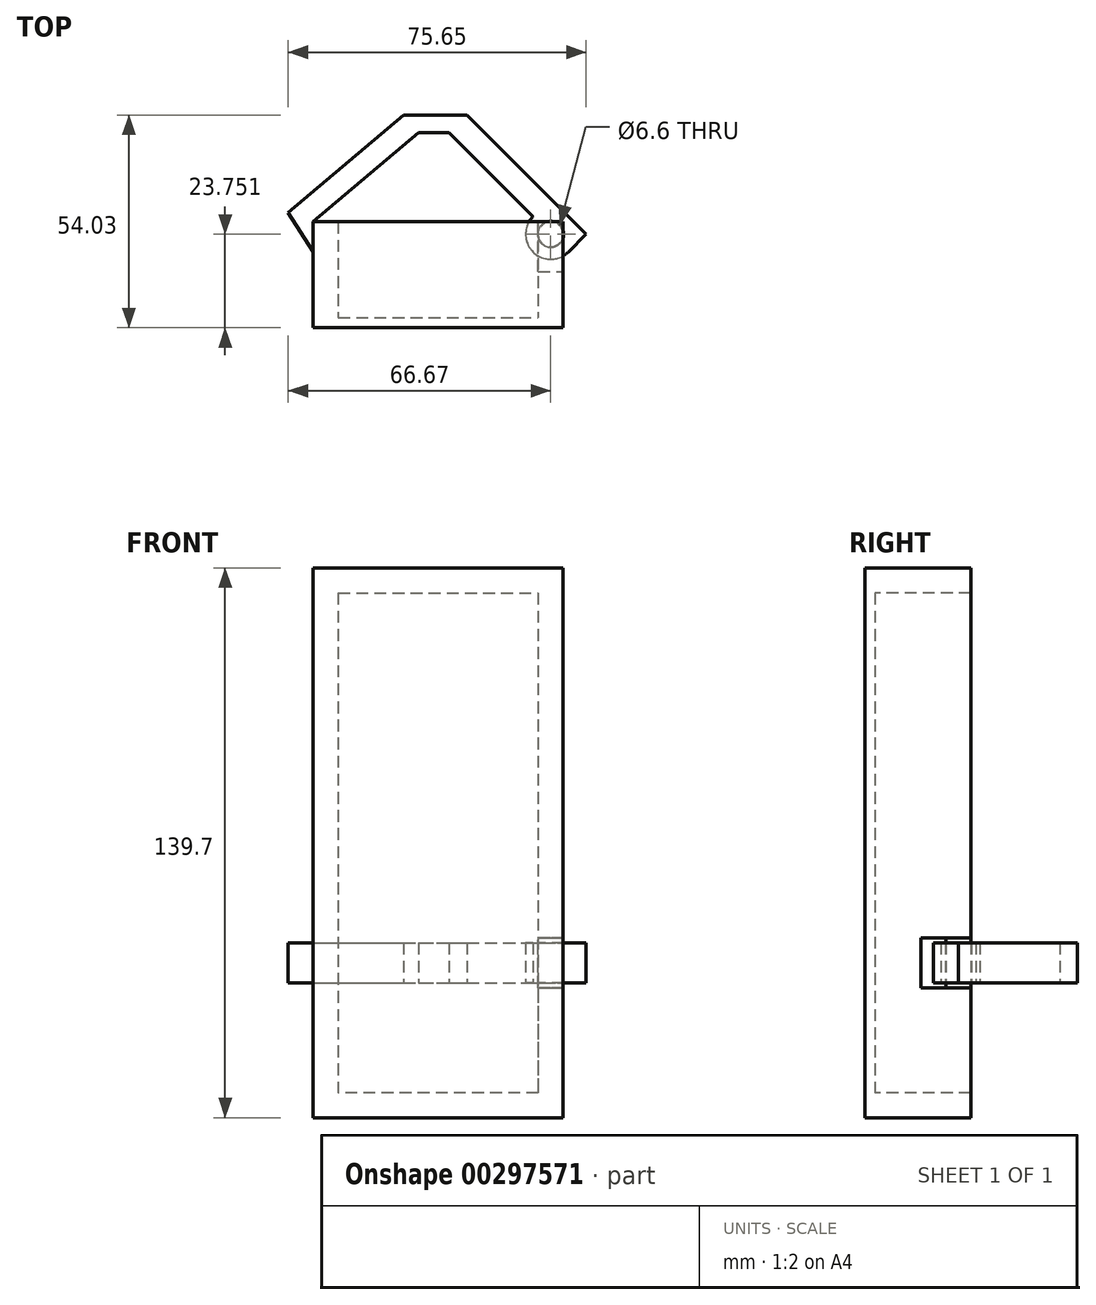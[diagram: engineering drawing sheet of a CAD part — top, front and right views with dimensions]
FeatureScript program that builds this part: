
annotation { "Feature Type Name" : "Feature", "Feature Type Description" : "" }
export const myFeature = defineFeature(function(context is Context, id is Id, definition is map)
    precondition{}
    {
        {
            var Q0;
            Q0=qCreatedBy(makeId("Top.planeOp"),FACE);
            var sketch = newSketch(context, id + "F0", { "sketchPlane" : qUnion([Q0])});
            skLineSegment(sketch, "E0.bottom", {"start": v(-24.64, -17.12) * mm, "end": v(26.16, -17.12) * mm});
            skLineSegment(sketch, "E0.top", {"start": v(-24.64, -19.66) * mm, "end": v(26.16, -19.66) * mm});
            skLineSegment(sketch, "E0.left", {"start": v(-24.64, -17.12) * mm, "end": v(-24.64, -19.66) * mm});
            skLineSegment(sketch, "E0.right", {"start": v(26.16, -17.12) * mm, "end": v(26.16, -19.66) * mm});
            skLineSegment(sketch, "E1.bottom", {"start": v(-31, 7.27) * mm, "end": v(-24.64, 7.27) * mm});
            skLineSegment(sketch, "E1.top", {"start": v(-31, -19.66) * mm, "end": v(-24.64, -19.66) * mm});
            skLineSegment(sketch, "E1.left", {"start": v(-31, 7.27) * mm, "end": v(-31, -19.66) * mm});
            skLineSegment(sketch, "E1.right", {"start": v(-24.64, 7.27) * mm, "end": v(-24.64, -19.66) * mm});
            skLineSegment(sketch, "E2.bottom", {"start": v(26.16, 7.27) * mm, "end": v(32.5, 7.27) * mm});
            skLineSegment(sketch, "E2.top", {"start": v(26.16, -19.66) * mm, "end": v(32.5, -19.66) * mm});
            skLineSegment(sketch, "E2.left", {"start": v(26.16, 7.27) * mm, "end": v(26.16, -19.66) * mm});
            skLineSegment(sketch, "E2.right", {"start": v(32.5, 7.27) * mm, "end": v(32.5, -19.66) * mm});
            skSolve(sketch);
        }
        {
            var Q0;
            Q0 = qSketchRegion(id + "F0", true);
            extrude(context, id + "F1", {"entities" : qUnion([Q0]), "depth" : 127 * mm});
        }
        {
            var Q0;
            Q0=makeQuery(id+"F1.opExtrude","CAP_FACE",FACE,{"disambiguationData":[OSD([sQuery(id+"F0.wireOp",EDGE,"E0.bottom"),sQuery(id+"F0.wireOp",EDGE,"E0.top"),sQuery(id+"F0.wireOp",EDGE,"E1.bottom"),sQuery(id+"F0.wireOp",EDGE,"E1.top"),sQuery(id+"F0.wireOp",EDGE,"E1.left"),sQuery(id+"F0.wireOp",EDGE,"E1.right"),sQuery(id+"F0.wireOp",EDGE,"E2.bottom"),sQuery(id+"F0.wireOp",EDGE,"E2.top"),sQuery(id+"F0.wireOp",EDGE,"E2.left"),sQuery(id+"F0.wireOp",EDGE,"E2.right")])],"isStart":true});
            var sketch = newSketch(context, id + "F2", { "sketchPlane" : qUnion([Q0])});
            skLineSegment(sketch, "E3.bottom", {"start": v(32.5, -7.27) * mm, "end": v(-31, -7.27) * mm});
            skLineSegment(sketch, "E3.top", {"start": v(32.5, 19.66) * mm, "end": v(-31, 19.66) * mm});
            skLineSegment(sketch, "E3.left", {"start": v(32.5, -7.27) * mm, "end": v(32.5, 19.66) * mm});
            skLineSegment(sketch, "E3.right", {"start": v(-31, -7.27) * mm, "end": v(-31, 19.66) * mm});
            skSolve(sketch);
        }
        {
            var Q0;
            Q0 = qSketchRegion(id + "F2", true);
            extrude(context, id + "F3", {"entities" : qUnion([Q0]), "operationType" : NewBodyOperationType.ADD, "depth" : 6.35 * mm});
        }
        {
            var Q0;
            Q0=makeQuery(id+"F1.opExtrude","CAP_FACE",FACE,{"disambiguationData":[OSD([sQuery(id+"F0.wireOp",EDGE,"E0.bottom"),sQuery(id+"F0.wireOp",EDGE,"E0.top"),sQuery(id+"F0.wireOp",EDGE,"E1.bottom"),sQuery(id+"F0.wireOp",EDGE,"E1.top"),sQuery(id+"F0.wireOp",EDGE,"E1.left"),sQuery(id+"F0.wireOp",EDGE,"E1.right"),sQuery(id+"F0.wireOp",EDGE,"E2.bottom"),sQuery(id+"F0.wireOp",EDGE,"E2.top"),sQuery(id+"F0.wireOp",EDGE,"E2.left"),sQuery(id+"F0.wireOp",EDGE,"E2.right")])],"isStart":false});
            var sketch = newSketch(context, id + "F4", { "sketchPlane" : qUnion([Q0])});
            skLineSegment(sketch, "E4.bottom", {"start": v(-31, 7.27) * mm, "end": v(32.5, 7.27) * mm});
            skLineSegment(sketch, "E4.top", {"start": v(-31, -19.66) * mm, "end": v(32.5, -19.66) * mm});
            skLineSegment(sketch, "E4.left", {"start": v(-31, 7.27) * mm, "end": v(-31, -19.66) * mm});
            skLineSegment(sketch, "E4.right", {"start": v(32.5, 7.27) * mm, "end": v(32.5, -19.66) * mm});
            skSolve(sketch);
        }
        {
            var Q0;
            Q0 = qSketchRegion(id + "F4", true);
            extrude(context, id + "F5", {"entities" : qUnion([Q0]), "operationType" : NewBodyOperationType.ADD, "depth" : 6.35 * mm});
        }
        {
            var Q0;
            Q0=makeQuery(id+"F5.boolean.opBoolean","MERGE",FACE,{"derivedFrom":[makeQuery(id+"F3.boolean.opBoolean","MERGE",FACE,{"derivedFrom":[makeQuery(id+"F1.opExtrude","SWEPT_FACE",FACE,{"disambiguationData":[OSD([sQuery(id+"F0.wireOp",EDGE,"E2.right")])]}),makeQuery(id+"F3.opExtrude","SWEPT_FACE",FACE,{"disambiguationData":[OSD([sQuery(id+"F2.wireOp",EDGE,"E3.left")])]})]}),makeQuery(id+"F5.opExtrude","SWEPT_FACE",FACE,{"disambiguationData":[OSD([sQuery(id+"F4.wireOp",EDGE,"E4.right")])]})]});
            var sketch = newSketch(context, id + "F6", { "sketchPlane" : qUnion([Q0])});
            skLineSegment(sketch, "E5.bottom", {"start": v(7.27, 39.37) * mm, "end": v(-5.43, 39.37) * mm});
            skLineSegment(sketch, "E5.top", {"start": v(7.27, 26.67) * mm, "end": v(-5.43, 26.67) * mm});
            skLineSegment(sketch, "E5.left", {"start": v(7.27, 39.37) * mm, "end": v(7.27, 26.67) * mm});
            skLineSegment(sketch, "E5.right", {"start": v(-5.43, 39.37) * mm, "end": v(-5.43, 26.67) * mm});
            skSolve(sketch);
        }
        {
            var Q0;
            Q0 = qSketchRegion(id + "F6", true);
            extrude(context, id + "F7", {"entities" : qUnion([Q0]), "operationType" : NewBodyOperationType.REMOVE, "endBound" : BoundingType.UP_TO_NEXT, "oppositeDirection" : true, "depth" : 25 * mm});
        }
        {
            var Q0;
            Q0=makeQuery(id+"F7.boolean.opBoolean","COPY",FACE,{"derivedFrom":makeQuery(id+"F7.opExtrude","SWEPT_FACE",FACE,{"disambiguationData":[OSD([sQuery(id+"F6.wireOp",EDGE,"E5.top")])]})});
            var sketch = newSketch(context, id + "F8", { "sketchPlane" : qUnion([Q0])});
            skCircle(sketch, "E6", {"center": v(29.33, 4.1) * mm, "radius": 3.18 * mm});
            skSolve(sketch);
        }
        {
            var Q0;
            Q0 = qSketchRegion(id + "F8", true);
            extrude(context, id + "F9", {"entities" : qUnion([Q0]), "operationType" : NewBodyOperationType.ADD, "endBound" : BoundingType.UP_TO_NEXT, "depth" : 25 * mm});
        }
        {
            var Q0;
            {var subQ0=makeQuery(id+"F7.boolean.opBoolean","COPY",FACE,{"derivedFrom":makeQuery(id+"F7.opExtrude","SWEPT_FACE",FACE,{"disambiguationData":[OSD([sQuery(id+"F6.wireOp",EDGE,"E5.top")])]})});Q0=makeQuery(id+"F9.boolean.opBoolean","SPLIT",FACE,{"disambiguationData":[TD([makeQuery(id+"F1.opExtrude","SWEPT_FACE",FACE,{"disambiguationData":[OSD([sQuery(id+"F0.wireOp",EDGE,"E2.left")])]}),makeQuery(id+"F1.opExtrude","SWEPT_FACE",FACE,{"disambiguationData":[OSD([sQuery(id+"F0.wireOp",EDGE,"E2.right")])]}),makeQuery(id+"F3.opExtrude","SWEPT_FACE",FACE,{"disambiguationData":[OSD([sQuery(id+"F2.wireOp",EDGE,"E3.left")])]}),makeQuery(id+"F5.opExtrude","SWEPT_FACE",FACE,{"disambiguationData":[OSD([sQuery(id+"F4.wireOp",EDGE,"E4.right")])]}),subQ0,makeQuery(id+"F7.boolean.opBoolean","COPY",FACE,{"derivedFrom":makeQuery(id+"F7.opExtrude","SWEPT_FACE",FACE,{"disambiguationData":[OSD([sQuery(id+"F6.wireOp",EDGE,"E5.right")])]})}),makeQuery(id+"F9.opExtrude","SWEPT_FACE",FACE,{"disambiguationData":[OSD([sQuery(id+"F8.wireOp",EDGE,"E6")])]})])],"derivedFrom":subQ0});}
            var sketch = newSketch(context, id + "F10", { "sketchPlane" : qUnion([Q0])});
            skCircle(sketch, "E7", {"center": v(29.33, 4.1) * mm, "radius": 3.3 * mm});
            skCircle(sketch, "E8", {"center": v(29.33, 4.1) * mm, "radius": 6.35 * mm});
            skLineSegment(sketch, "E9.bottom", {"start": v(8.03, 34.37) * mm, "end": v(38.31, 4.1) * mm});
            skLineSegment(sketch, "E9.top", {"start": v(3.54, 29.88) * mm, "end": v(33.82, -0.4) * mm});
            skLineSegment(sketch, "E9.left", {"start": v(8.03, 34.37) * mm, "end": v(3.54, 29.88) * mm});
            skLineSegment(sketch, "E9.right", {"start": v(38.31, 4.1) * mm, "end": v(33.82, -0.4) * mm});
            skLineSegment(sketch, "E10.bottom", {"start": v(-8.03, 34.37) * mm, "end": v(8.03, 34.37) * mm});
            skLineSegment(sketch, "E10.top", {"start": v(-8.03, 29.88) * mm, "end": v(8.03, 29.88) * mm});
            skLineSegment(sketch, "E10.left", {"start": v(-8.03, 34.37) * mm, "end": v(-8.03, 29.88) * mm});
            skLineSegment(sketch, "E10.right", {"start": v(8.03, 34.37) * mm, "end": v(8.03, 29.88) * mm});
            skLineSegment(sketch, "E11.bottom", {"start": v(-37.34, 9.6) * mm, "end": v(-8.03, 34.37) * mm});
            skLineSegment(sketch, "E11.top", {"start": v(-33.55, 5.1) * mm, "end": v(-4.23, 29.88) * mm});
            skLineSegment(sketch, "E11.left", {"start": v(-37.34, 9.6) * mm, "end": v(-33.55, 5.1) * mm});
            skLineSegment(sketch, "E11.right", {"start": v(-8.03, 34.37) * mm, "end": v(-4.23, 29.88) * mm});
            skPoint(sketch, "E12", {"position": v(0, 34.37) * mm});
            skLineSegment(sketch, "E13", {"start": v(-37.34, 9.6) * mm, "end": v(-31, -0.35) * mm});
            skLineSegment(sketch, "E14", {"start": v(-31, -0.35) * mm, "end": v(-31, 7.27) * mm});
            skLineSegment(sketch, "E15.bottom", {"start": v(-31, -0.35) * mm, "end": v(-28.45, -0.35) * mm});
            skLineSegment(sketch, "E15.top", {"start": v(-31, 2.19) * mm, "end": v(-28.45, 2.19) * mm});
            skLineSegment(sketch, "E15.left", {"start": v(-31, -0.35) * mm, "end": v(-31, 2.19) * mm});
            skLineSegment(sketch, "E15.right", {"start": v(-28.45, -0.35) * mm, "end": v(-28.45, 2.19) * mm});
            skSolve(sketch);
        }
        {
            var Q0;
            Q0 = qSketchRegion(id + "F10", true);
            extrude(context, id + "F11", {"entities" : qUnion([Q0]), "operationType" : NewBodyOperationType.ADD, "depth" : 11.43 * mm, "hasSecondDirection" : true, "secondDirectionOppositeDirection" : false, "secondDirectionDepth" : 1.27 * mm});
        }
    });
